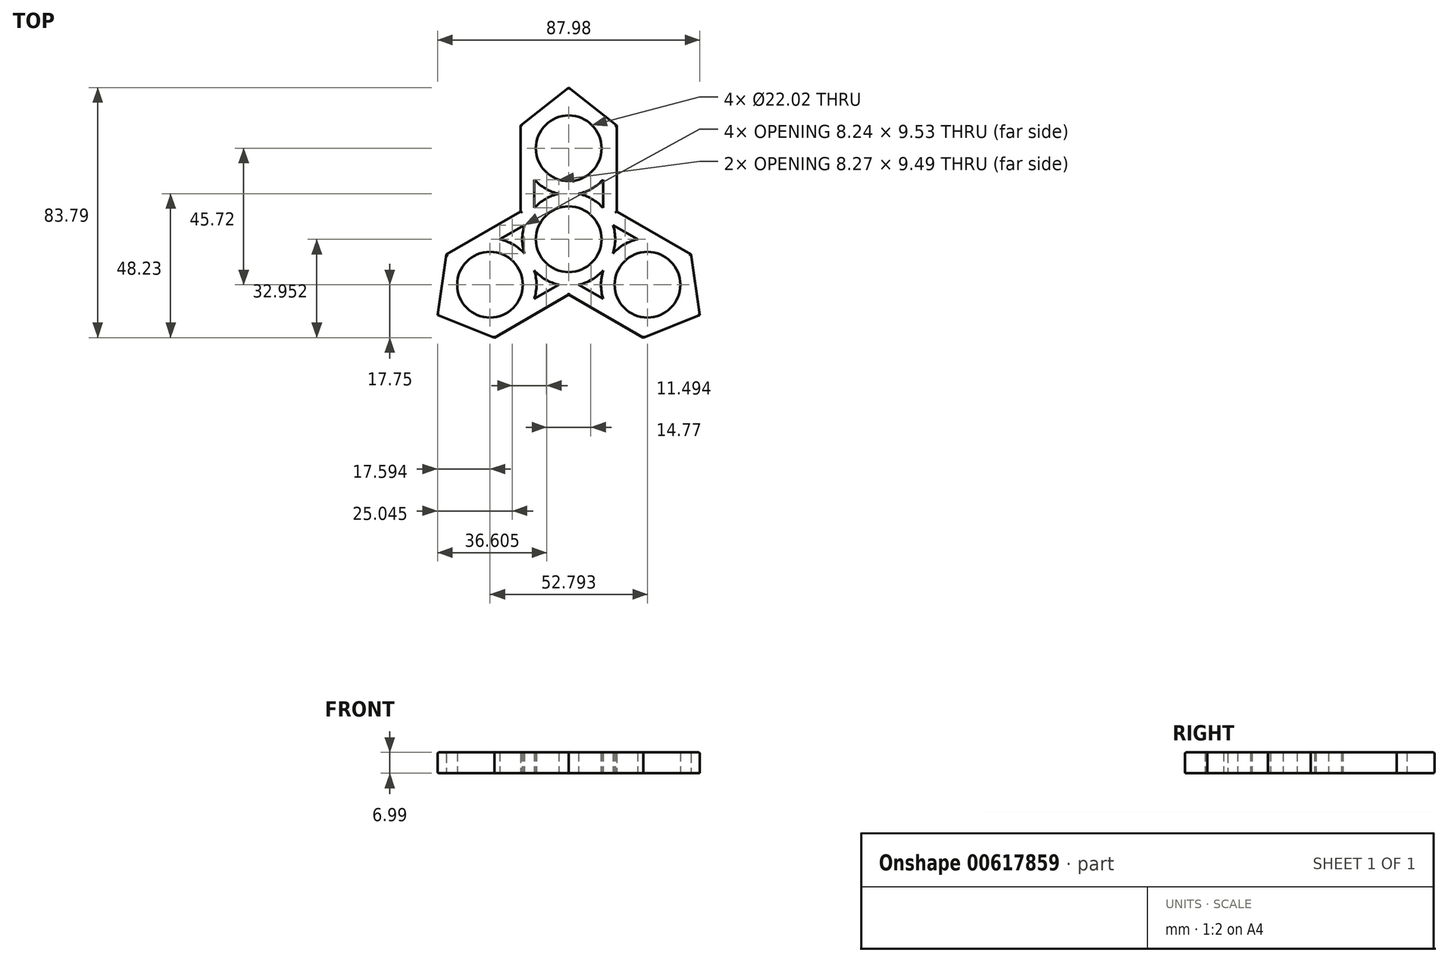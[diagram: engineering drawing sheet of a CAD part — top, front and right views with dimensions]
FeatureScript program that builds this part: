
annotation { "Feature Type Name" : "Feature", "Feature Type Description" : "" }
export const myFeature = defineFeature(function(context is Context, id is Id, definition is map)
    precondition{}
    {
        {
            var Q0;
            Q0=qCreatedBy(makeId("Top.planeOp"),FACE);
            var sketch = newSketch(context, id + "F0", { "sketchPlane" : qUnion([Q0])});
            skCircle(sketch, "E0", {"center": v(0, 0) * mm, "radius": 11.01 * mm});
            skLineSegment(sketch, "E1", {"start": v(0, 0) * mm, "end": v(-26.4, -15.24) * mm});
            skLineSegment(sketch, "E2", {"start": v(0, 0) * mm, "end": v(26.4, -15.24) * mm});
            skLineSegment(sketch, "E3", {"start": v(0, 0) * mm, "end": v(0, 30.48) * mm});
            skCircle(sketch, "E4", {"center": v(0, 30.48) * mm, "radius": 11.01 * mm});
            skCircle(sketch, "E5", {"center": v(-26.4, -15.24) * mm, "radius": 11.01 * mm});
            skCircle(sketch, "E6", {"center": v(26.4, -15.24) * mm, "radius": 11.01 * mm});
            skCircle(sketch, "E7", {"center": v(0, 0) * mm, "radius": 16.1 * mm});
            skLineSegment(sketch, "E8", {"start": v(-20.9, -24.78) * mm, "end": v(-4.66, -15.4) * mm});
            skLineSegment(sketch, "E9.0", {"start": v(-24.95, -32.99) * mm, "end": v(8.05, -13.94) * mm});
            skLineSegment(sketch, "E10", {"start": v(4.66, -15.4) * mm, "end": v(20.9, -24.78) * mm});
            skLineSegment(sketch, "E11.0", {"start": v(-8.05, -13.94) * mm, "end": v(24.95, -32.99) * mm});
            skPoint(sketch, "E12", {"position": v(0, -18.58) * mm});
            skLineSegment(sketch, "E13", {"start": v(-24.95, -32.99) * mm, "end": v(-41.04, -5.11) * mm});
            skLineSegment(sketch, "E14", {"start": v(-31.9, -5.7) * mm, "end": v(-15.67, 3.67) * mm});
            skLineSegment(sketch, "E15.0", {"start": v(-41.04, -5.11) * mm, "end": v(-8.05, 13.94) * mm});
            skLineSegment(sketch, "E16", {"start": v(15.67, 3.67) * mm, "end": v(31.9, -5.7) * mm});
            skLineSegment(sketch, "E17.0", {"start": v(8.05, 13.94) * mm, "end": v(41.04, -5.11) * mm});
            skLineSegment(sketch, "E18", {"start": v(24.95, -32.99) * mm, "end": v(41.04, -5.11) * mm});
            skLineSegment(sketch, "E19", {"start": v(-11.01, 30.48) * mm, "end": v(-11.01, 11.73) * mm});
            skLineSegment(sketch, "E20", {"start": v(11.01, 30.48) * mm, "end": v(11.01, 11.73) * mm});
            skLineSegment(sketch, "E21.0", {"start": v(-16.1, 38.1) * mm, "end": v(-16.1, 0) * mm});
            skLineSegment(sketch, "E22.0", {"start": v(16.1, 38.1) * mm, "end": v(16.1, 0) * mm});
            skLineSegment(sketch, "E23", {"start": v(-16.1, 38.1) * mm, "end": v(16.1, 38.1) * mm});
            skPoint(sketch, "E24", {"position": v(-16.1, 9.3) * mm});
            skPoint(sketch, "E25", {"position": v(16.1, 9.3) * mm});
            skLineSegment(sketch, "E26.0", {"start": v(44, -25.4) * mm, "end": v(24.95, -32.99) * mm});
            skLineSegment(sketch, "E26.2", {"start": v(41.04, -5.11) * mm, "end": v(44, -25.4) * mm});
            skLineSegment(sketch, "E27", {"start": v(-16.1, 38.1) * mm, "end": v(0, 50.8) * mm});
            skLineSegment(sketch, "E28", {"start": v(0, 50.8) * mm, "end": v(16.1, 38.1) * mm});
            skLineSegment(sketch, "E29", {"start": v(-41.04, -5.11) * mm, "end": v(-44, -25.4) * mm});
            skLineSegment(sketch, "E30", {"start": v(-44, -25.4) * mm, "end": v(-24.95, -32.99) * mm});
            skSolve(sketch);
        }
        {
            var Q0;
            Q0 = qSketchRegion(id + "F0", true);
            var Q1;
            {var subQ7=sQuery(id+"F0.wireOp",EDGE,"E1");var subQ8=sQuery(id+"F0.wireOp",EDGE,"E0");var subQ9=makeQuery(id+"F0.imprint","INTERSECT",VERTEX,{"derivedFrom":[subQ8,subQ7]});Q1=makeQuery(id+"F0.imprint","IMPRINT",FACE,{"disambiguationData":[TD([[makeQuery(id+"F0.imprint","IMPRINT",EDGE,{"disambiguationData":[TD([[subQ9,1.0]])],"derivedFrom":subQ8}),-1.0]])]});}
            var Q2;
            {var subQ1=sQuery(id+"F0.wireOp",EDGE,"E3");var subQ5=sQuery(id+"F0.wireOp",EDGE,"E0");var subQ6=makeQuery(id+"F0.imprint","INTERSECT",VERTEX,{"derivedFrom":[subQ5,subQ1]});Q2=makeQuery(id+"F0.imprint","IMPRINT",FACE,{"disambiguationData":[TD([[makeQuery(id+"F0.imprint","IMPRINT",EDGE,{"disambiguationData":[TD([[subQ6,1.0]])],"derivedFrom":subQ5}),-1.0]])]});}
            var Q3;
            {var subQ1=sQuery(id+"F0.wireOp",EDGE,"E0");var subQ9=sQuery(id+"F0.wireOp",EDGE,"E1");var subQ10=makeQuery(id+"F0.imprint","INTERSECT",VERTEX,{"derivedFrom":[subQ1,subQ9]});Q3=makeQuery(id+"F0.imprint","IMPRINT",FACE,{"disambiguationData":[TD([[makeQuery(id+"F0.imprint","IMPRINT",EDGE,{"disambiguationData":[TD([[subQ10,-1.0]])],"derivedFrom":subQ1}),-1.0]])]});}
            var Q4;
            {var subQ0=sQuery(id+"F0.wireOp",EDGE,"E10");var subQ1=sQuery(id+"F0.wireOp",EDGE,"E6");var subQ2=makeQuery(id+"F0.imprint","INTERSECT",VERTEX,{"derivedFrom":[subQ1,subQ0]});Q4=makeQuery(id+"F0.imprint","IMPRINT",FACE,{"disambiguationData":[TD([[makeQuery(id+"F0.imprint","IMPRINT",EDGE,{"disambiguationData":[TD([[subQ2,1.0]])],"derivedFrom":subQ1}),-1.0]])]});}
            var Q5;
            {var subQ0=sQuery(id+"F0.wireOp",EDGE,"E8");var subQ1=sQuery(id+"F0.wireOp",EDGE,"E5");var subQ2=makeQuery(id+"F0.imprint","INTERSECT",VERTEX,{"derivedFrom":[subQ1,subQ0]});Q5=makeQuery(id+"F0.imprint","IMPRINT",FACE,{"disambiguationData":[TD([[makeQuery(id+"F0.imprint","IMPRINT",EDGE,{"disambiguationData":[TD([[subQ2,-1.0]])],"derivedFrom":subQ1}),-1.0]])]});}
            var Q6;
            {var subQ0=sQuery(id+"F0.wireOp",EDGE,"E16");var subQ1=sQuery(id+"F0.wireOp",EDGE,"E6");var subQ2=makeQuery(id+"F0.imprint","INTERSECT",VERTEX,{"derivedFrom":[subQ1,subQ0]});Q6=makeQuery(id+"F0.imprint","IMPRINT",FACE,{"disambiguationData":[TD([[makeQuery(id+"F0.imprint","IMPRINT",EDGE,{"disambiguationData":[TD([[subQ2,-1.0]])],"derivedFrom":subQ1}),-1.0]])]});}
            var Q7;
            {var subQ0=sQuery(id+"F0.wireOp",EDGE,"E20");var subQ1=sQuery(id+"F0.wireOp",EDGE,"E4");var subQ2=makeQuery(id+"F0.imprint","INTERSECT",VERTEX,{"derivedFrom":[subQ1,subQ0]});Q7=makeQuery(id+"F0.imprint","IMPRINT",FACE,{"disambiguationData":[TD([[makeQuery(id+"F0.imprint","IMPRINT",EDGE,{"disambiguationData":[TD([[subQ2,1.0]])],"derivedFrom":subQ1}),-1.0]])]});}
            var Q8;
            {var subQ0=sQuery(id+"F0.wireOp",EDGE,"E19");var subQ1=sQuery(id+"F0.wireOp",EDGE,"E4");var subQ2=makeQuery(id+"F0.imprint","INTERSECT",VERTEX,{"derivedFrom":[subQ1,subQ0]});Q8=makeQuery(id+"F0.imprint","IMPRINT",FACE,{"disambiguationData":[TD([[makeQuery(id+"F0.imprint","IMPRINT",EDGE,{"disambiguationData":[TD([[subQ2,-1.0]])],"derivedFrom":subQ1}),-1.0]])]});}
            var Q9;
            {var subQ0=sQuery(id+"F0.wireOp",EDGE,"E14");var subQ1=sQuery(id+"F0.wireOp",EDGE,"E5");var subQ2=makeQuery(id+"F0.imprint","INTERSECT",VERTEX,{"derivedFrom":[subQ1,subQ0]});Q9=makeQuery(id+"F0.imprint","IMPRINT",FACE,{"disambiguationData":[TD([[makeQuery(id+"F0.imprint","IMPRINT",EDGE,{"disambiguationData":[TD([[subQ2,1.0]])],"derivedFrom":subQ1}),-1.0]])]});}
            var Q10;
            {var subQ0=sQuery(id+"F0.wireOp",EDGE,"E16");var subQ1=sQuery(id+"F0.wireOp",EDGE,"E7");var subQ2=makeQuery(id+"F0.imprint","INTERSECT",VERTEX,{"derivedFrom":[subQ1,subQ0]});Q10=makeQuery(id+"F0.imprint","IMPRINT",FACE,{"disambiguationData":[TD([[makeQuery(id+"F0.imprint","IMPRINT",EDGE,{"disambiguationData":[TD([[subQ2,1.0]])],"derivedFrom":subQ1}),-1.0]])]});}
            var Q11;
            {var subQ0=sQuery(id+"F0.wireOp",EDGE,"E17.0");var subQ1=sQuery(id+"F0.wireOp",EDGE,"E7");var subQ2=makeQuery(id+"F0.imprint","INTERSECT",VERTEX,{"derivedFrom":[subQ1,subQ0]});Q11=makeQuery(id+"F0.imprint","IMPRINT",FACE,{"disambiguationData":[TD([[makeQuery(id+"F0.imprint","IMPRINT",EDGE,{"disambiguationData":[TD([[subQ2,1.0]])],"derivedFrom":subQ1}),-1.0]])]});}
            var Q12;
            {var subQ0=sQuery(id+"F0.wireOp",EDGE,"E15.0");var subQ1=sQuery(id+"F0.wireOp",EDGE,"E7");var subQ2=makeQuery(id+"F0.imprint","INTERSECT",VERTEX,{"derivedFrom":[subQ1,subQ0]});Q12=makeQuery(id+"F0.imprint","IMPRINT",FACE,{"disambiguationData":[TD([[makeQuery(id+"F0.imprint","IMPRINT",EDGE,{"disambiguationData":[TD([[subQ2,-1.0]])],"derivedFrom":subQ1}),-1.0]])]});}
            var Q13;
            {var subQ0=sQuery(id+"F0.wireOp",EDGE,"E14");var subQ1=sQuery(id+"F0.wireOp",EDGE,"E7");var subQ2=makeQuery(id+"F0.imprint","INTERSECT",VERTEX,{"derivedFrom":[subQ1,subQ0]});Q13=makeQuery(id+"F0.imprint","IMPRINT",FACE,{"disambiguationData":[TD([[makeQuery(id+"F0.imprint","IMPRINT",EDGE,{"disambiguationData":[TD([[subQ2,-1.0]])],"derivedFrom":subQ1}),-1.0]])]});}
            var Q14;
            {var subQ0=sQuery(id+"F0.wireOp",EDGE,"E8");var subQ1=sQuery(id+"F0.wireOp",EDGE,"E7");var subQ2=makeQuery(id+"F0.imprint","INTERSECT",VERTEX,{"derivedFrom":[subQ1,subQ0]});Q14=makeQuery(id+"F0.imprint","IMPRINT",FACE,{"disambiguationData":[TD([[makeQuery(id+"F0.imprint","IMPRINT",EDGE,{"disambiguationData":[TD([[subQ2,1.0]])],"derivedFrom":subQ1}),-1.0]])]});}
            var Q15;
            {var subQ0=sQuery(id+"F0.wireOp",EDGE,"E9.0");var subQ1=sQuery(id+"F0.wireOp",EDGE,"E7");var subQ2=makeQuery(id+"F0.imprint","INTERSECT",VERTEX,{"derivedFrom":[subQ1,subQ0]});Q15=makeQuery(id+"F0.imprint","IMPRINT",FACE,{"disambiguationData":[TD([[makeQuery(id+"F0.imprint","IMPRINT",EDGE,{"disambiguationData":[TD([[subQ2,1.0]])],"derivedFrom":subQ1}),-1.0]])]});}
            extrude(context, id + "F1", {"entities" : qUnion([Q0, Q1, Q2, Q3, Q4, Q5, Q6, Q7, Q8, Q9, Q10, Q11, Q12, Q13, Q14, Q15]), "depth" : 7 * mm, "offsetDistance" : 25.4 * mm});
        }
        {
            var Q0;
            Q0=makeQuery(id+"F1.opExtrude","CAP_FACE",FACE,{"disambiguationData":[OSD([sQuery(id+"F0.wireOp",EDGE,"E0"),sQuery(id+"F0.wireOp",EDGE,"E4"),sQuery(id+"F0.wireOp",EDGE,"E5"),sQuery(id+"F0.wireOp",EDGE,"E6"),sQuery(id+"F0.wireOp",EDGE,"E9.0"),sQuery(id+"F0.wireOp",EDGE,"E11.0"),sQuery(id+"F0.wireOp",EDGE,"E15.0"),sQuery(id+"F0.wireOp",EDGE,"E17.0"),sQuery(id+"F0.wireOp",EDGE,"E21.0"),sQuery(id+"F0.wireOp",EDGE,"E22.0"),sQuery(id+"F0.wireOp",EDGE,"E26.0"),sQuery(id+"F0.wireOp",EDGE,"E26.2"),sQuery(id+"F0.wireOp",EDGE,"E27"),sQuery(id+"F0.wireOp",EDGE,"E28"),sQuery(id+"F0.wireOp",EDGE,"E29"),sQuery(id+"F0.wireOp",EDGE,"E30")])],"isStart":true});
            var Q1;
            Q1=makeQuery(id+"F1.opExtrude","CAP_FACE",FACE,{"disambiguationData":[OSD([sQuery(id+"F0.wireOp",EDGE,"E0"),sQuery(id+"F0.wireOp",EDGE,"E4"),sQuery(id+"F0.wireOp",EDGE,"E5"),sQuery(id+"F0.wireOp",EDGE,"E6"),sQuery(id+"F0.wireOp",EDGE,"E9.0"),sQuery(id+"F0.wireOp",EDGE,"E11.0"),sQuery(id+"F0.wireOp",EDGE,"E15.0"),sQuery(id+"F0.wireOp",EDGE,"E17.0"),sQuery(id+"F0.wireOp",EDGE,"E21.0"),sQuery(id+"F0.wireOp",EDGE,"E22.0"),sQuery(id+"F0.wireOp",EDGE,"E26.0"),sQuery(id+"F0.wireOp",EDGE,"E26.2"),sQuery(id+"F0.wireOp",EDGE,"E27"),sQuery(id+"F0.wireOp",EDGE,"E28"),sQuery(id+"F0.wireOp",EDGE,"E29"),sQuery(id+"F0.wireOp",EDGE,"E30")])],"isStart":false});
            shell(context, id + "F2", {"entities" : qUnion([Q0, Q1]), "thickness" : 4.57 * mm});
        }
        {
            var Q0;
            Q0=makeQuery(id+"F1.opExtrude","CAP_EDGE",EDGE,{"disambiguationData":[OSD([sQuery(id+"F0.wireOp",EDGE,"E21.0")])],"isStart":false});
            var Q1;
            Q1=makeQuery(id+"F1.opExtrude","CAP_EDGE",EDGE,{"disambiguationData":[OSD([sQuery(id+"F0.wireOp",EDGE,"E27")])],"isStart":false});
            var Q2;
            Q2=makeQuery(id+"F1.opExtrude","CAP_EDGE",EDGE,{"disambiguationData":[OSD([sQuery(id+"F0.wireOp",EDGE,"E28")])],"isStart":false});
            var Q3;
            Q3=makeQuery(id+"F1.opExtrude","CAP_EDGE",EDGE,{"disambiguationData":[OSD([sQuery(id+"F0.wireOp",EDGE,"E22.0")])],"isStart":false});
            var Q4;
            Q4=makeQuery(id+"F1.opExtrude","CAP_EDGE",EDGE,{"disambiguationData":[OSD([sQuery(id+"F0.wireOp",EDGE,"E17.0")])],"isStart":false});
            var Q5;
            Q5=makeQuery(id+"F1.opExtrude","CAP_EDGE",EDGE,{"disambiguationData":[OSD([sQuery(id+"F0.wireOp",EDGE,"E26.2")])],"isStart":false});
            var Q6;
            Q6=makeQuery(id+"F1.opExtrude","CAP_EDGE",EDGE,{"disambiguationData":[OSD([sQuery(id+"F0.wireOp",EDGE,"E26.0")])],"isStart":false});
            var Q7;
            Q7=makeQuery(id+"F1.opExtrude","CAP_EDGE",EDGE,{"disambiguationData":[OSD([sQuery(id+"F0.wireOp",EDGE,"E11.0")])],"isStart":false});
            var Q8;
            Q8=makeQuery(id+"F1.opExtrude","CAP_EDGE",EDGE,{"disambiguationData":[OSD([sQuery(id+"F0.wireOp",EDGE,"E9.0")])],"isStart":false});
            var Q9;
            Q9=makeQuery(id+"F1.opExtrude","CAP_EDGE",EDGE,{"disambiguationData":[OSD([sQuery(id+"F0.wireOp",EDGE,"E30")])],"isStart":false});
            var Q10;
            Q10=makeQuery(id+"F1.opExtrude","CAP_EDGE",EDGE,{"disambiguationData":[OSD([sQuery(id+"F0.wireOp",EDGE,"E29")])],"isStart":false});
            var Q11;
            Q11=makeQuery(id+"F1.opExtrude","CAP_EDGE",EDGE,{"disambiguationData":[OSD([sQuery(id+"F0.wireOp",EDGE,"E15.0")])],"isStart":false});
            fillet(context, id + "F3", {"entities" : qUnion([Q0, Q1, Q2, Q3, Q4, Q5, Q6, Q7, Q8, Q9, Q10, Q11]), "radius" : 0.5 * mm, "tangentPropagation" : true, "allowEdgeOverflow" : false});
        }
        {
            var Q0;
            Q0=makeQuery(id+"F1.opExtrude","CAP_EDGE",EDGE,{"disambiguationData":[OSD([sQuery(id+"F0.wireOp",EDGE,"E9.0")])],"isStart":true});
            var Q1;
            Q1=makeQuery(id+"F1.opExtrude","CAP_EDGE",EDGE,{"disambiguationData":[OSD([sQuery(id+"F0.wireOp",EDGE,"E11.0")])],"isStart":true});
            var Q2;
            Q2=makeQuery(id+"F1.opExtrude","CAP_EDGE",EDGE,{"disambiguationData":[OSD([sQuery(id+"F0.wireOp",EDGE,"E17.0")])],"isStart":true});
            var Q3;
            Q3=makeQuery(id+"F1.opExtrude","CAP_EDGE",EDGE,{"disambiguationData":[OSD([sQuery(id+"F0.wireOp",EDGE,"E22.0")])],"isStart":true});
            var Q4;
            Q4=makeQuery(id+"F1.opExtrude","CAP_EDGE",EDGE,{"disambiguationData":[OSD([sQuery(id+"F0.wireOp",EDGE,"E21.0")])],"isStart":true});
            var Q5;
            Q5=makeQuery(id+"F1.opExtrude","CAP_EDGE",EDGE,{"disambiguationData":[OSD([sQuery(id+"F0.wireOp",EDGE,"E15.0")])],"isStart":true});
            var Q6;
            Q6=makeQuery(id+"F1.opExtrude","CAP_EDGE",EDGE,{"disambiguationData":[OSD([sQuery(id+"F0.wireOp",EDGE,"E29")])],"isStart":true});
            var Q7;
            Q7=makeQuery(id+"F1.opExtrude","CAP_EDGE",EDGE,{"disambiguationData":[OSD([sQuery(id+"F0.wireOp",EDGE,"E30")])],"isStart":true});
            var Q8;
            Q8=makeQuery(id+"F1.opExtrude","CAP_EDGE",EDGE,{"disambiguationData":[OSD([sQuery(id+"F0.wireOp",EDGE,"E26.0")])],"isStart":true});
            var Q9;
            Q9=makeQuery(id+"F1.opExtrude","CAP_EDGE",EDGE,{"disambiguationData":[OSD([sQuery(id+"F0.wireOp",EDGE,"E26.2")])],"isStart":true});
            var Q10;
            Q10=makeQuery(id+"F1.opExtrude","CAP_EDGE",EDGE,{"disambiguationData":[OSD([sQuery(id+"F0.wireOp",EDGE,"E28")])],"isStart":true});
            var Q11;
            Q11=makeQuery(id+"F1.opExtrude","CAP_EDGE",EDGE,{"disambiguationData":[OSD([sQuery(id+"F0.wireOp",EDGE,"E27")])],"isStart":true});
            fillet(context, id + "F4", {"entities" : qUnion([Q0, Q1, Q2, Q3, Q4, Q5, Q6, Q7, Q8, Q9, Q10, Q11]), "radius" : 0.5 * mm, "tangentPropagation" : true, "allowEdgeOverflow" : false});
        }
    });
